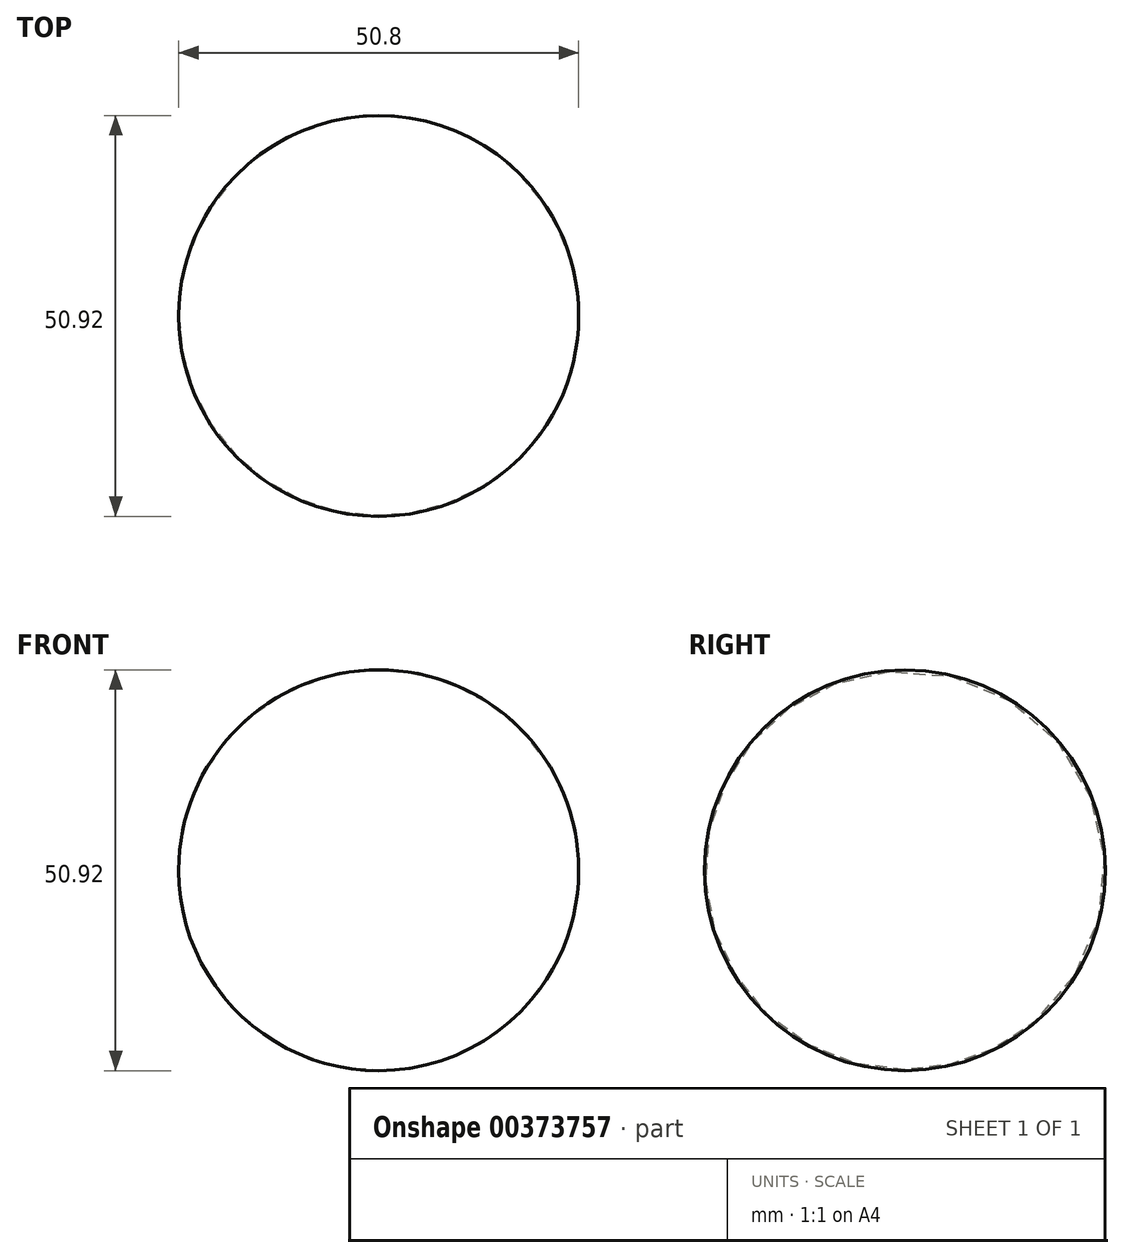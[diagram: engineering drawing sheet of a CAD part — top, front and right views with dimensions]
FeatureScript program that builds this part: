
annotation { "Feature Type Name" : "Feature", "Feature Type Description" : "" }
export const myFeature = defineFeature(function(context is Context, id is Id, definition is map)
    precondition{}
    {
        {
            var Q0;
            Q0=qCreatedBy(makeId("Top.planeOp"),FACE);
            var sketch = newSketch(context, id + "F0", { "sketchPlane" : qUnion([Q0])});
            skLineSegment(sketch, "E0", {"start": v(-24.38, 0) * mm, "end": v(26.42, 0) * mm});
            skArc(sketch, "E1", {"start": v(26.42, 0) * mm, "mid": v(1.02, 25.34) * mm, "end": v(-24.38, 0) * mm});
            skSolve(sketch);
        }
        {
            var Q0;
            Q0=makeQuery(id+"F0.imprint","IMPRINT",FACE,{"disambiguationData":[TD([[makeQuery(id+"F0.imprint","IMPRINT",EDGE,{"derivedFrom":sQuery(id+"F0.wireOp",EDGE,"E0")}),1.0]])]});
            var Q1;
            Q1=sQuery(id+"F0.wireOp",EDGE,"E0");
            revolve(context, id + "F1", {"entities" : qUnion([Q0]), "axis" : qUnion([Q1]), "revolveType" : RevolveType.FULL});
        }
    });
